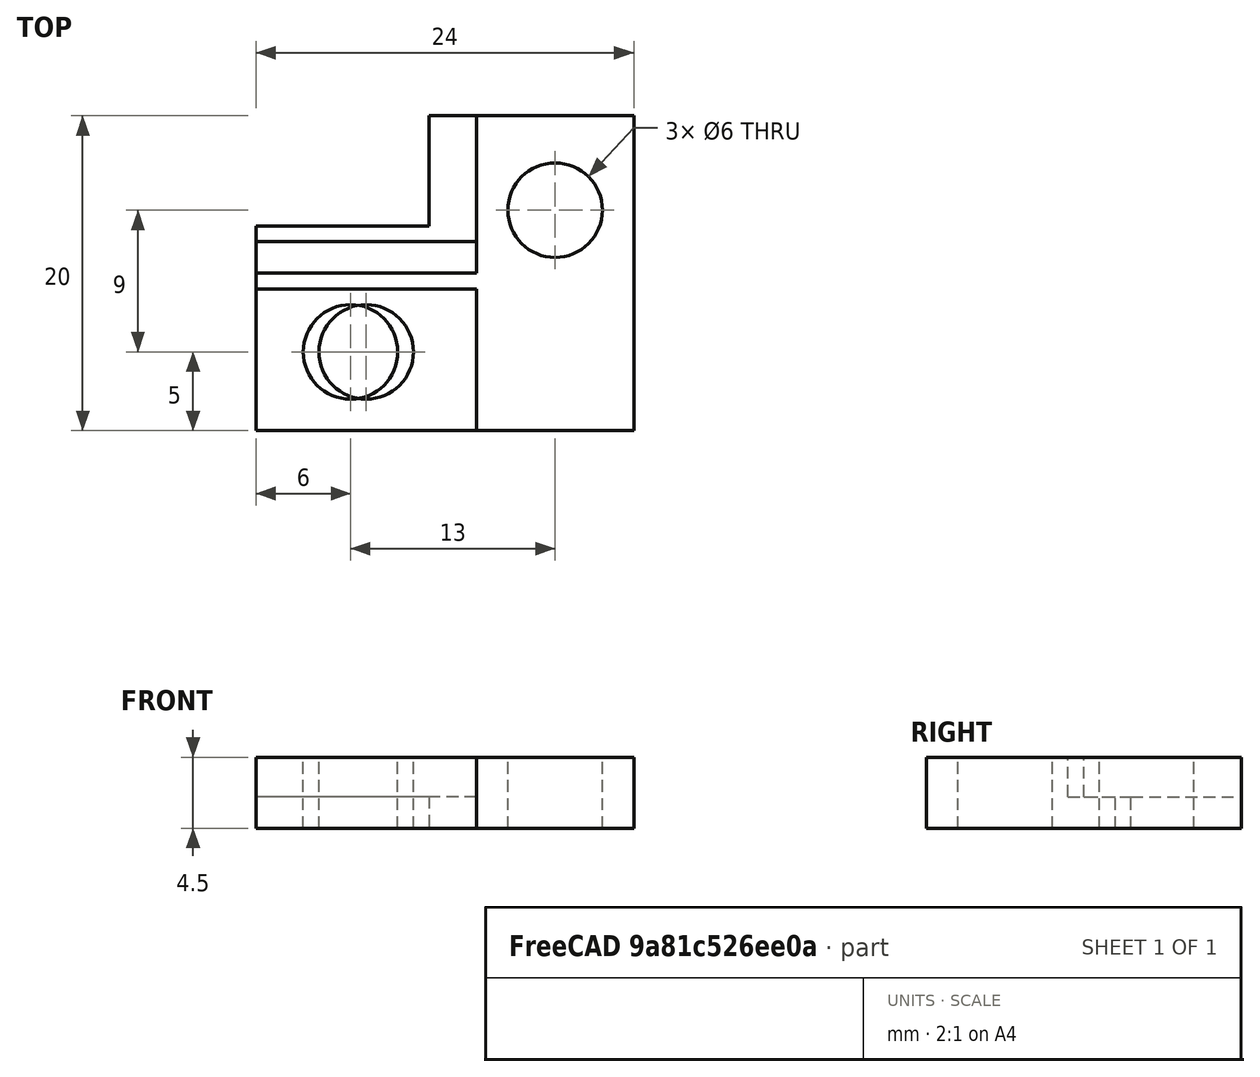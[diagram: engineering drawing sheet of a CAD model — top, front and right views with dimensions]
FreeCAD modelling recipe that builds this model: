
FCSTD DOCUMENT  (FreeCAD 0.18.4R)
Label: holder
License: All rights reserved
LicenseURL: http://en.wikipedia.org/wiki/All_rights_reserved
objects: Part::Box×6, Part::Cylinder×3, Part::MultiFuse×3, Part::Cut×2
note: 14 computed .brp shape members not serialized (recipe doc carries the construction recipe); baked Part::Feature solids carry a one-line shape summary decoded from their .brp

FEATURE [Part::Box] Box  label="Cube"
  AttacherType = Attacher::AttachEngine3D
  Height = 2
  Length = 14
  Width = 12
FEATURE [Part::Box] Box001  label="Cube001"
  AttacherType = Attacher::AttachEngine3D
  Height = 4.5
  Length = 14
  Width = 9
FEATURE [Part::Cylinder] Cylinder
  Angle = 360
  AttacherType = Attacher::AttachEngine3D
  Height = 10
  Placement = pos=(7,5,-1) rot=(0,0,1;0rad)
  Radius = 3
FEATURE [Part::MultiFuse] Fusion
  Shapes = -> [Box,Box001]
FEATURE [Part::Cut] Cut  label="linear"
  Base = -> Fusion
  Tool = -> Cylinder
FEATURE [Part::Box] Box002  label="Cube002"
  AttacherType = Attacher::AttachEngine3D
  Height = 4.5
  Length = 14
  Width = 10
FEATURE [Part::Cylinder] Cylinder001
  Angle = 360
  AttacherType = Attacher::AttachEngine3D
  Height = 10
  Placement = pos=(6,5,-1) rot=(0,0,1;0rad)
  Radius = 3
FEATURE [Part::Box] Box003  label="Cube003"
  AttacherType = Attacher::AttachEngine3D
  Height = 2
  Length = 14
  Width = 13
FEATURE [Part::Box] Box004  label="Cube004"
  AttacherType = Attacher::AttachEngine3D
  Height = 2
  Length = 13
  Placement = pos=(11,0,0) rot=(0,0,1;0rad)
  Width = 20
FEATURE [Part::Box] Box005  label="Cube005"
  AttacherType = Attacher::AttachEngine3D
  Height = 4.5
  Length = 10
  Placement = pos=(14,0,0) rot=(0,0,1;0rad)
  Width = 20
FEATURE [Part::Cylinder] Cylinder002
  Angle = 360
  AttacherType = Attacher::AttachEngine3D
  Height = 10
  Placement = pos=(19,14,-1) rot=(0,0,1;0rad)
  Radius = 3
FEATURE [Part::MultiFuse] Fusion001
  Shapes = -> [Cylinder001,Cylinder002]
FEATURE [Part::MultiFuse] Fusion002
  Shapes = -> [Box003,Box002,Box004,Box005]
FEATURE [Part::Cut] Cut001  label="angular"
  Base = -> Fusion002
  Tool = -> Fusion001
